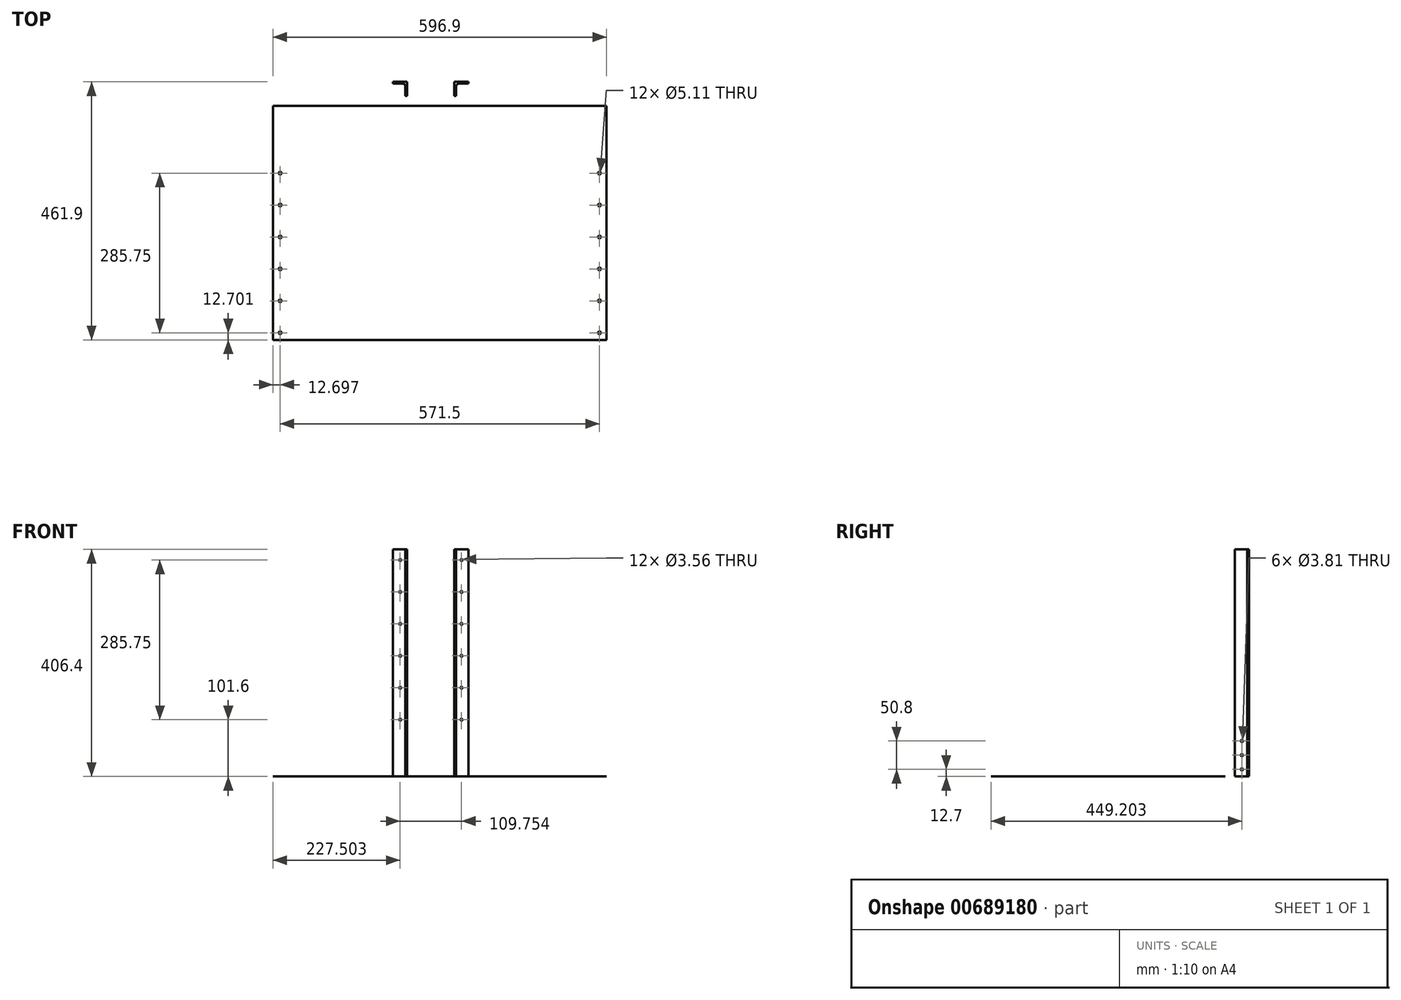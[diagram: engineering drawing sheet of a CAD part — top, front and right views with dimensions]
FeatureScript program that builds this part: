
annotation { "Feature Type Name" : "Feature", "Feature Type Description" : "" }
export const myFeature = defineFeature(function(context is Context, id is Id, definition is map)
    precondition{}
    {
        {
            var Q0;
            Q0=qCreatedBy(makeId("Top.planeOp"),FACE);
            var sketch = newSketch(context, id + "F0", { "sketchPlane" : qUnion([Q0])});
            skLineSegment(sketch, "E0", {"start": v(42.18, 19.58) * mm, "end": v(42.18, 44.98) * mm});
            skLineSegment(sketch, "E1", {"start": v(42.18, 44.98) * mm, "end": v(67.58, 44.98) * mm});
            skLineSegment(sketch, "E2", {"start": v(67.58, 44.98) * mm, "end": v(67.58, 41.8) * mm});
            skLineSegment(sketch, "E3", {"start": v(67.58, 41.8) * mm, "end": v(45.35, 41.8) * mm});
            skLineSegment(sketch, "E4", {"start": v(45.35, 41.8) * mm, "end": v(45.35, 19.58) * mm});
            skLineSegment(sketch, "E5", {"start": v(45.35, 19.58) * mm, "end": v(42.18, 19.58) * mm});
            skSolve(sketch);
        }
        {
            var Q0;
            Q0=makeQuery(id+"F0.imprint","IMPRINT",FACE,{"disambiguationData":[TD([[makeQuery(id+"F0.imprint","IMPRINT",EDGE,{"derivedFrom":sQuery(id+"F0.wireOp",EDGE,"E0")}),-1.0]])]});
            extrude(context, id + "F1", {"entities" : qUnion([Q0]), "depth" : 406.4 * mm, "offsetDistance" : 25.4 * mm});
        }
        {
            var Q0;
            Q0=makeQuery(id+"F1.opExtrude","SWEPT_EDGE",EDGE,{"disambiguationData":[OSD([sQuery(id+"F0.wireOp",EDGE,"E3"),sQuery(id+"F0.wireOp",EDGE,"E4")])]});
            fillet(context, id + "F2", {"entities" : qUnion([Q0]), "radius" : 5.08 * mm, "tangentPropagation" : true, "allowEdgeOverflow" : false});
        }
        {
            var Q0;
            Q0=makeQuery(id+"F1.opExtrude","SWEPT_FACE",FACE,{"disambiguationData":[OSD([sQuery(id+"F0.wireOp",EDGE,"E0")])]});
            var sketch = newSketch(context, id + "F3", { "sketchPlane" : qUnion([Q0])});
            skCircle(sketch, "E6", {"center": v(-32.28, 12.7) * mm, "radius": 1.9 * mm});
            skCircle(sketch, "E7", {"center": v(-32.28, 38.1) * mm, "radius": 1.9 * mm});
            skCircle(sketch, "E8", {"center": v(-32.28, 63.5) * mm, "radius": 1.9 * mm});
            skLineSegment(sketch, "E9", {"start": v(-32.28, 63.5) * mm, "end": v(-32.28, 38.1) * mm, "construction": true});
            skLineSegment(sketch, "E10", {"start": v(-32.28, 12.7) * mm, "end": v(-32.28, 38.1) * mm, "construction": true});
            skPoint(sketch, "E11", {"position": v(-32.28, 0) * mm});
            skSolve(sketch);
        }
        {
            var Q0;
            Q0 = qSketchRegion(id + "F3", true);
            extrude(context, id + "F4", {"entities" : qUnion([Q0]), "operationType" : NewBodyOperationType.REMOVE, "endBound" : BoundingType.THROUGH_ALL, "oppositeDirection" : true, "depth" : 25.4 * mm, "offsetDistance" : 25.4 * mm});
        }
        {
            var Q0;
            Q0=makeQuery(id+"F1.opExtrude","SWEPT_FACE",FACE,{"disambiguationData":[OSD([sQuery(id+"F0.wireOp",EDGE,"E1")])]});
            var sketch = newSketch(context, id + "F5", { "sketchPlane" : qUnion([Q0])});
            skCircle(sketch, "E12", {"center": v(-54.88, 101.6) * mm, "radius": 1.78 * mm});
            skPoint(sketch, "E12.centerSnap0", {"position": v(-54.88, 0) * mm});
            skCircle(sketch, "E13.0.1.0", {"center": v(-54.88, 158.75) * mm, "radius": 1.78 * mm});
            skCircle(sketch, "E13.0.2.0", {"center": v(-54.88, 215.9) * mm, "radius": 1.78 * mm});
            skCircle(sketch, "E13.0.3.0", {"center": v(-54.88, 273.05) * mm, "radius": 1.78 * mm});
            skCircle(sketch, "E13.0.4.0", {"center": v(-54.88, 330.2) * mm, "radius": 1.78 * mm});
            skLineSegment(sketch, "E13.direction1", {"start": v(-54.88, 101.6) * mm, "end": v(-54.88, 101.6) * mm});
            skLineSegment(sketch, "E13.direction2", {"start": v(-54.88, 101.6) * mm, "end": v(-54.88, 158.75) * mm, "construction": true});
            skCircle(sketch, "E14.0.0.5", {"center": v(-54.88, 387.35) * mm, "radius": 1.78 * mm});
            skSolve(sketch);
        }
        {
            var Q0;
            Q0 = qSketchRegion(id + "F5", true);
            extrude(context, id + "F6", {"entities" : qUnion([Q0]), "operationType" : NewBodyOperationType.REMOVE, "endBound" : BoundingType.THROUGH_ALL, "oppositeDirection" : true, "depth" : 25.4 * mm, "offsetDistance" : 25.4 * mm});
        }
        {
            var Q0;
            Q0=makeQuery(id+"F1.opExtrude","SWEPT_BODY",BODY,{"disambiguationData":[OSD([sQuery(id+"F0.wireOp",EDGE,"E0"),sQuery(id+"F0.wireOp",EDGE,"E1"),sQuery(id+"F0.wireOp",EDGE,"E2"),sQuery(id+"F0.wireOp",EDGE,"E3"),sQuery(id+"F0.wireOp",EDGE,"E4"),sQuery(id+"F0.wireOp",EDGE,"E5")])]});
            var Q1;
            Q1=qCreatedBy(makeId("Right.planeOp"),FACE);
            mirror(context, id + "F7", {"entities" : qUnion([Q0]), "mirrorPlane" : qUnion([Q1])});
        }
        {
            var Q0;
            Q0=qCreatedBy(makeId("Top.planeOp"),FACE);
            var sketch = newSketch(context, id + "F8", { "sketchPlane" : qUnion([Q0])});
            skLineSegment(sketch, "E15.bottom", {"start": v(-282.38, 2.18) * mm, "end": v(314.52, 2.18) * mm});
            skLineSegment(sketch, "E15.top", {"start": v(-282.38, -416.92) * mm, "end": v(314.52, -416.92) * mm});
            skLineSegment(sketch, "E15.left", {"start": v(-282.38, 2.18) * mm, "end": v(-282.38, -416.92) * mm});
            skLineSegment(sketch, "E15.right", {"start": v(314.52, 2.18) * mm, "end": v(314.52, -416.92) * mm});
            skPoint(sketch, "E15.middle", {"position": v(16.07, -207.37) * mm});
            skLineSegment(sketch, "E16", {"start": v(16.07, 2.18) * mm, "end": v(16.07, -416.92) * mm, "construction": true});
            skCircle(sketch, "E17", {"center": v(-269.68, -404.22) * mm, "radius": 2.55 * mm});
            skCircle(sketch, "E18.0.1.0", {"center": v(-269.68, -347.07) * mm, "radius": 2.55 * mm});
            skCircle(sketch, "E18.0.2.0", {"center": v(-269.68, -289.92) * mm, "radius": 2.55 * mm});
            skCircle(sketch, "E18.0.3.0", {"center": v(-269.68, -232.77) * mm, "radius": 2.55 * mm});
            skCircle(sketch, "E18.0.4.0", {"center": v(-269.68, -175.62) * mm, "radius": 2.55 * mm});
            skCircle(sketch, "E18.0.5.0", {"center": v(-269.68, -118.47) * mm, "radius": 2.55 * mm});
            skLineSegment(sketch, "E18.direction1", {"start": v(-269.68, -404.22) * mm, "end": v(-244.28, -404.22) * mm, "construction": true});
            skLineSegment(sketch, "E18.direction2", {"start": v(-269.68, -404.22) * mm, "end": v(-269.68, -347.07) * mm, "construction": true});
            skCircle(sketch, "E19.MirrorC", {"center": v(301.82, -404.22) * mm, "radius": 2.55 * mm});
            skCircle(sketch, "E20.MirrorC", {"center": v(301.82, -347.07) * mm, "radius": 2.55 * mm});
            skCircle(sketch, "E21.MirrorC", {"center": v(301.82, -175.62) * mm, "radius": 2.55 * mm});
            skCircle(sketch, "E22.MirrorC", {"center": v(301.82, -289.92) * mm, "radius": 2.55 * mm});
            skCircle(sketch, "E23.MirrorC", {"center": v(301.82, -118.47) * mm, "radius": 2.55 * mm});
            skCircle(sketch, "E24.MirrorC", {"center": v(301.82, -232.77) * mm, "radius": 2.55 * mm});
            skSolve(sketch);
        }
        {
            var Q0;
            Q0=makeQuery(id+"F8.imprint","IMPRINT",FACE,{"disambiguationData":[TD([[makeQuery(id+"F8.imprint","IMPRINT",EDGE,{"derivedFrom":sQuery(id+"F8.wireOp",EDGE,"E15.bottom")}),-1.0]])]});
            extrude(context, id + "F9", {"entities" : qUnion([Q0]), "depth" : 1 / 203.2 * mm, "offsetDistance" : 25.4 * mm});
        }
    });
